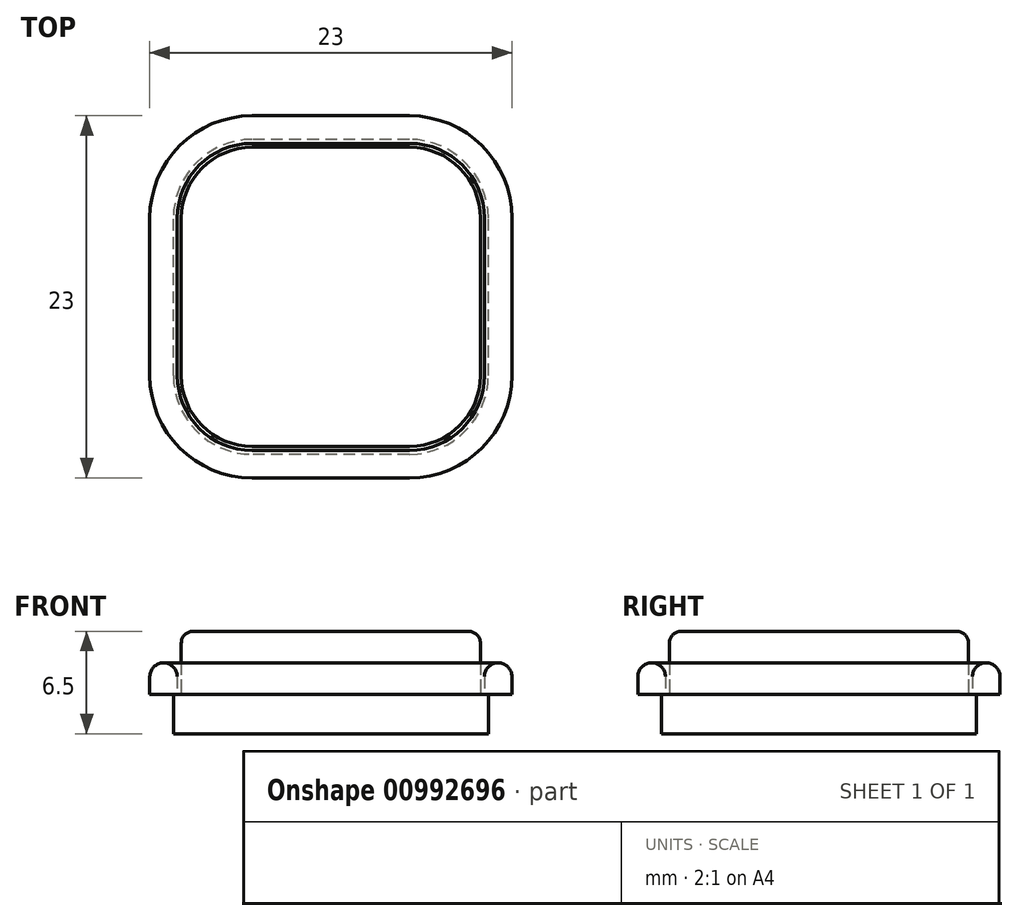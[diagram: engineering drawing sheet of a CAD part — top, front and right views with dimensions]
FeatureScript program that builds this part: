
annotation { "Feature Type Name" : "Feature", "Feature Type Description" : "" }
export const myFeature = defineFeature(function(context is Context, id is Id, definition is map)
    precondition{}
    {
        {
            var Q0;
            Q0=qCreatedBy(makeId("Top.planeOp"),FACE);
            var sketch = newSketch(context, id + "F0", { "sketchPlane" : qUnion([Q0])});
            skLineSegment(sketch, "E0.bottom", {"start": v(5, -10) * mm, "end": v(-5, -10) * mm});
            skLineSegment(sketch, "E0.top", {"start": v(5, 10) * mm, "end": v(-5, 10) * mm});
            skLineSegment(sketch, "E0.left", {"start": v(10, -5) * mm, "end": v(10, 5) * mm});
            skLineSegment(sketch, "E0.right", {"start": v(-10, -5) * mm, "end": v(-10, 5) * mm});
            skPoint(sketch, "E0.middle", {"position": v(0, 0) * mm});
            skPoint(sketch, "E1.visualSharp", {"position": v(-10, 10) * mm});
            skArc(sketch, "E1.filletArc", {"start": v(-5, 10) * mm, "mid": v(-8.54, 8.54) * mm, "end": v(-10, 5) * mm});
            skPoint(sketch, "E2.visualSharp", {"position": v(10, 10) * mm});
            skArc(sketch, "E2.filletArc", {"start": v(10, 5) * mm, "mid": v(8.54, 8.54) * mm, "end": v(5, 10) * mm});
            skPoint(sketch, "E3.visualSharp", {"position": v(10, -10) * mm});
            skArc(sketch, "E3.filletArc", {"start": v(5, -10) * mm, "mid": v(8.54, -8.54) * mm, "end": v(10, -5) * mm});
            skPoint(sketch, "E4.visualSharp", {"position": v(-10, -10) * mm});
            skArc(sketch, "E4.filletArc", {"start": v(-10, -5) * mm, "mid": v(-8.54, -8.54) * mm, "end": v(-5, -10) * mm});
            skSolve(sketch);
        }
        {
            var Q0;
            Q0 = qSketchRegion(id + "F0", true);
            extrude(context, id + "F1", {"entities" : qUnion([Q0]), "depth" : 2.5 * mm, "offsetDistance" : 25 * mm});
        }
        {
            var Q0;
            Q0=makeQuery(id+"F1.opExtrude","CAP_FACE",FACE,{"disambiguationData":[OSD([sQuery(id+"F0.wireOp",EDGE,"E0.bottom"),sQuery(id+"F0.wireOp",EDGE,"E0.top"),sQuery(id+"F0.wireOp",EDGE,"E0.left"),sQuery(id+"F0.wireOp",EDGE,"E0.right"),sQuery(id+"F0.wireOp",EDGE,"E1.filletArc"),sQuery(id+"F0.wireOp",EDGE,"E2.filletArc"),sQuery(id+"F0.wireOp",EDGE,"E3.filletArc"),sQuery(id+"F0.wireOp",EDGE,"E4.filletArc")])],"isStart":false});
            var sketch = newSketch(context, id + "F2", { "sketchPlane" : qUnion([Q0])});
            skLineSegment(sketch, "E5.bottom", {"start": v(5, -11.5) * mm, "end": v(-5, -11.5) * mm});
            skLineSegment(sketch, "E5.top", {"start": v(5, 11.5) * mm, "end": v(-5, 11.5) * mm});
            skLineSegment(sketch, "E5.left", {"start": v(11.5, -5) * mm, "end": v(11.5, 5) * mm});
            skLineSegment(sketch, "E5.right", {"start": v(-11.5, -5) * mm, "end": v(-11.5, 5) * mm});
            skPoint(sketch, "E5.middle", {"position": v(0, 0) * mm});
            skPoint(sketch, "E6.visualSharp", {"position": v(-10, 10) * mm});
            skPoint(sketch, "E7.visualSharp", {"position": v(10, 10) * mm});
            skPoint(sketch, "E8.visualSharp", {"position": v(10, -10) * mm});
            skPoint(sketch, "E9.visualSharp", {"position": v(-10, -10) * mm});
            skPoint(sketch, "E10.visualSharp", {"position": v(-11.5, 11.5) * mm});
            skArc(sketch, "E10.filletArc", {"start": v(-5, 11.5) * mm, "mid": v(-9.6, 9.6) * mm, "end": v(-11.5, 5) * mm});
            skPoint(sketch, "E11.visualSharp", {"position": v(11.5, 11.5) * mm});
            skArc(sketch, "E11.filletArc", {"start": v(11.5, 5) * mm, "mid": v(9.6, 9.6) * mm, "end": v(5, 11.5) * mm});
            skPoint(sketch, "E12.visualSharp", {"position": v(11.5, -11.5) * mm});
            skArc(sketch, "E12.filletArc", {"start": v(5, -11.5) * mm, "mid": v(9.6, -9.6) * mm, "end": v(11.5, -5) * mm});
            skPoint(sketch, "E13.visualSharp", {"position": v(-11.5, -11.5) * mm});
            skArc(sketch, "E13.filletArc", {"start": v(-11.5, -5) * mm, "mid": v(-9.6, -9.6) * mm, "end": v(-5, -11.5) * mm});
            skLineSegment(sketch, "E14.bottom", {"start": v(5, -9.75) * mm, "end": v(-5, -9.75) * mm});
            skLineSegment(sketch, "E14.top", {"start": v(5, 9.75) * mm, "end": v(-5, 9.75) * mm});
            skLineSegment(sketch, "E14.left", {"start": v(9.75, -5) * mm, "end": v(9.75, 5) * mm});
            skLineSegment(sketch, "E14.right", {"start": v(-9.75, -5) * mm, "end": v(-9.75, 5) * mm});
            skPoint(sketch, "E15.visualSharp", {"position": v(-9.75, 9.75) * mm});
            skArc(sketch, "E15.filletArc", {"start": v(-5, 9.75) * mm, "mid": v(-8.36, 8.36) * mm, "end": v(-9.75, 5) * mm});
            skPoint(sketch, "E16.visualSharp", {"position": v(9.75, 9.75) * mm});
            skArc(sketch, "E16.filletArc", {"start": v(9.75, 5) * mm, "mid": v(8.36, 8.36) * mm, "end": v(5, 9.75) * mm});
            skPoint(sketch, "E17.visualSharp", {"position": v(9.75, -9.75) * mm});
            skArc(sketch, "E17.filletArc", {"start": v(5, -9.75) * mm, "mid": v(8.36, -8.36) * mm, "end": v(9.75, -5) * mm});
            skPoint(sketch, "E18.visualSharp", {"position": v(-9.75, -9.75) * mm});
            skArc(sketch, "E18.filletArc", {"start": v(-9.75, -5) * mm, "mid": v(-8.36, -8.36) * mm, "end": v(-5, -9.75) * mm});
            skSolve(sketch);
        }
        {
            var Q0;
            Q0 = qSketchRegion(id + "F2", true);
            extrude(context, id + "F3", {"entities" : qUnion([Q0]), "operationType" : NewBodyOperationType.ADD, "depth" : 2 * mm, "offsetDistance" : 25 * mm});
        }
        {
            var Q0;
            Q0=makeQuery(id+"F3.opExtrude","CAP_EDGE",EDGE,{"disambiguationData":[OSD([sQuery(id+"F2.wireOp",EDGE,"E14.right")])],"isStart":false});
            var Q1;
            Q1=makeQuery(id+"F3.opExtrude","CAP_EDGE",EDGE,{"disambiguationData":[OSD([sQuery(id+"F2.wireOp",EDGE,"E5.right")])],"isStart":false});
            fillet(context, id + "F4", {"entities" : qUnion([Q0, Q1]), "radius" : .875 * mm, "tangentPropagation" : true, "allowEdgeOverflow" : false});
        }
        {
            var Q0;
            Q0=makeQuery(id+"F1.opExtrude","CAP_FACE",FACE,{"disambiguationData":[OSD([sQuery(id+"F0.wireOp",EDGE,"E0.bottom"),sQuery(id+"F0.wireOp",EDGE,"E0.top"),sQuery(id+"F0.wireOp",EDGE,"E0.left"),sQuery(id+"F0.wireOp",EDGE,"E0.right"),sQuery(id+"F0.wireOp",EDGE,"E1.filletArc"),sQuery(id+"F0.wireOp",EDGE,"E2.filletArc"),sQuery(id+"F0.wireOp",EDGE,"E3.filletArc"),sQuery(id+"F0.wireOp",EDGE,"E4.filletArc")])],"isStart":false});
            var sketch = newSketch(context, id + "F5", { "sketchPlane" : qUnion([Q0])});
            skLineSegment(sketch, "E19.bottom", {"start": v(5, 9.5) * mm, "end": v(-5, 9.5) * mm});
            skLineSegment(sketch, "E19.top", {"start": v(5, -9.5) * mm, "end": v(-5, -9.5) * mm});
            skLineSegment(sketch, "E19.left", {"start": v(9.5, 5) * mm, "end": v(9.5, -5) * mm});
            skLineSegment(sketch, "E19.right", {"start": v(-9.5, 5) * mm, "end": v(-9.5, -5) * mm});
            skPoint(sketch, "E19.middle", {"position": v(0, 0) * mm});
            skPoint(sketch, "E20.visualSharp", {"position": v(-9.5, 9.5) * mm});
            skArc(sketch, "E20.filletArc", {"start": v(-5, 9.5) * mm, "mid": v(-8.18, 8.18) * mm, "end": v(-9.5, 5) * mm});
            skPoint(sketch, "E21.visualSharp", {"position": v(9.5, 9.5) * mm});
            skArc(sketch, "E21.filletArc", {"start": v(9.5, 5) * mm, "mid": v(8.18, 8.18) * mm, "end": v(5, 9.5) * mm});
            skPoint(sketch, "E22.visualSharp", {"position": v(9.5, -9.5) * mm});
            skArc(sketch, "E22.filletArc", {"start": v(5, -9.5) * mm, "mid": v(8.18, -8.18) * mm, "end": v(9.5, -5) * mm});
            skPoint(sketch, "E23.visualSharp", {"position": v(-9.5, -9.5) * mm});
            skArc(sketch, "E23.filletArc", {"start": v(-9.5, -5) * mm, "mid": v(-8.18, -8.18) * mm, "end": v(-5, -9.5) * mm});
            skSolve(sketch);
        }
        {
            var Q0;
            Q0 = qSketchRegion(id + "F5", true);
            extrude(context, id + "F6", {"entities" : qUnion([Q0]), "operationType" : NewBodyOperationType.ADD, "depth" : 4 * mm, "offsetDistance" : 25 * mm});
        }
        {
            var Q0;
            Q0=makeQuery(id+"F6.opExtrude","CAP_EDGE",EDGE,{"disambiguationData":[OSD([sQuery(id+"F5.wireOp",EDGE,"E19.top")])],"isStart":false});
            fillet(context, id + "F7", {"entities" : qUnion([Q0]), "radius" : .75 * mm, "tangentPropagation" : true, "allowEdgeOverflow" : false});
        }
    });
